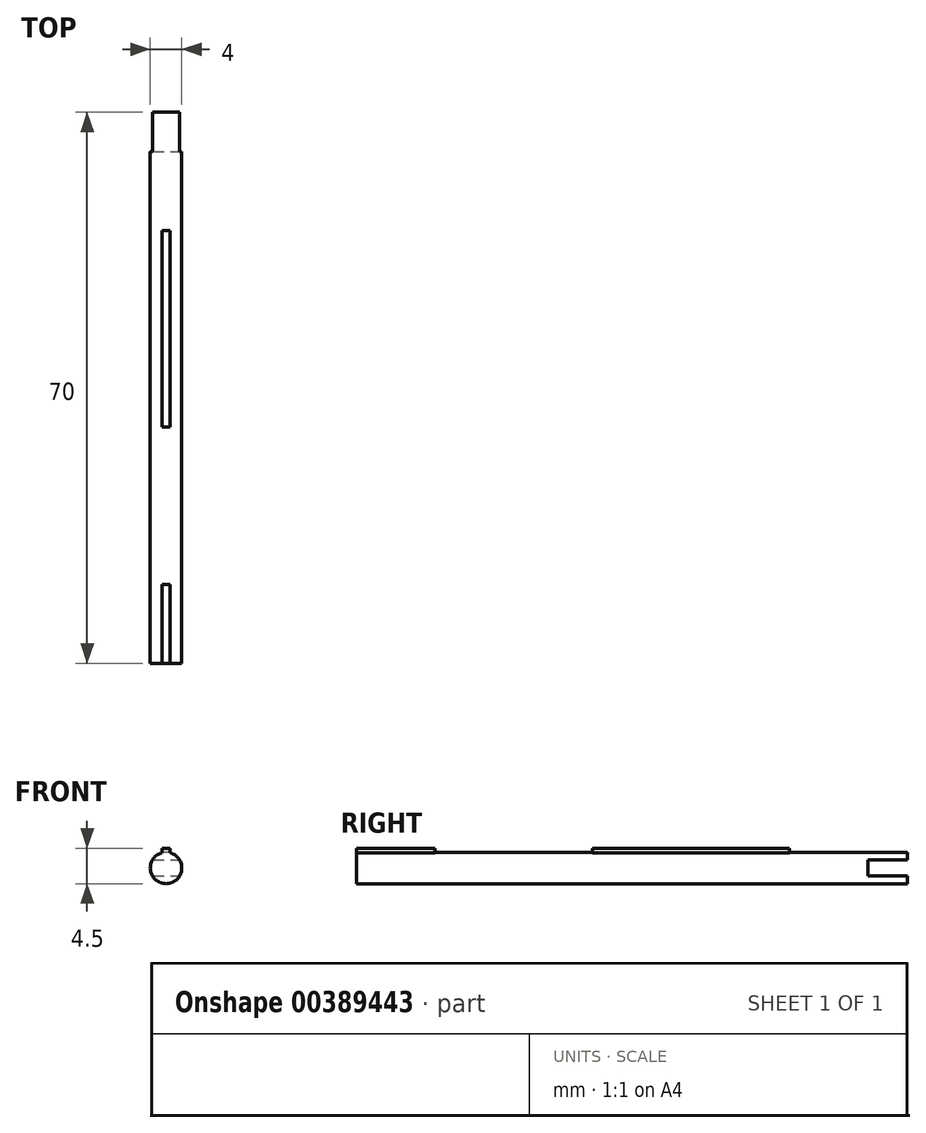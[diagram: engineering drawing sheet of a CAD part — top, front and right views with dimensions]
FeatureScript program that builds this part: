
annotation { "Feature Type Name" : "Feature", "Feature Type Description" : "" }
export const myFeature = defineFeature(function(context is Context, id is Id, definition is map)
    precondition{}
    {
        {
            var Q0;
            Q0=qCreatedBy(makeId("Front.planeOp"),FACE);
            var sketch = newSketch(context, id + "F0", { "sketchPlane" : qUnion([Q0])});
            skArc(sketch, "E0", {"start": v(-0.5, 1.94) * mm, "mid": v(0, -2) * mm, "end": v(0.5, 1.94) * mm});
            skLineSegment(sketch, "E1.bottom", {"start": v(0.5, 2.5) * mm, "end": v(-0.5, 2.5) * mm});
            skLineSegment(sketch, "E1.left", {"start": v(0.5, 2.5) * mm, "end": v(0.5, 1.94) * mm});
            skLineSegment(sketch, "E1.right", {"start": v(-0.5, 2.5) * mm, "end": v(-0.5, 1.94) * mm});
            skPoint(sketch, "E1.middle", {"position": v(0, 2) * mm});
            skPoint(sketch, "E2.orphan", {"position": v(-0.5, 1.5) * mm});
            skPoint(sketch, "E3.orphan", {"position": v(0.5, 1.5) * mm});
            skSolve(sketch);
        }
        {
            var Q0;
            Q0=qSketchRegion(id+"F0",true);
            var Q1;
            Q1=makeQuery(id+"F0.imprint","IMPRINT",FACE,{"disambiguationData":[TD([[makeQuery(id+"F0.imprint","IMPRINT",EDGE,{"derivedFrom":sQuery(id+"F0.wireOp",EDGE,"E0")}),1.0]])]});
            extrude(context, id + "F1", {"entities" : qUnion([Q0, Q1]), "depth" : 70 * mm});
        }
        {
            var Q0;
            Q0=makeQuery(id+"F1.opExtrude","CAP_FACE",FACE,{"disambiguationData":[OSD([sQuery(id+"F0.wireOp",EDGE,"E0"),sQuery(id+"F0.wireOp",EDGE,"E1.bottom"),sQuery(id+"F0.wireOp",EDGE,"E1.left"),sQuery(id+"F0.wireOp",EDGE,"E1.right")])],"isStart":false});
            cPlane(context, id + "F2", {"entities" : qUnion([Q0]), "cplaneType" : CPlaneType.OFFSET, "offset" : 10 * mm, "oppositeDirection" : true, "width" : 150 * mm, "height" : 150 * mm});
        }
        {
            var Q0;
            Q0=qCreatedBy(id+"F2.planeOp",FACE);
            var sketch = newSketch(context, id + "F3", { "sketchPlane" : qUnion([Q0])});
            skArc(sketch, "E4", {"start": v(0.5, 1.94) * mm, "mid": v(0, 2) * mm, "end": v(-0.5, 1.94) * mm});
            skLineSegment(sketch, "E5", {"start": v(-0.5, 2.5) * mm, "end": v(0.5, 2.5) * mm});
            skLineSegment(sketch, "E6", {"start": v(0.5, 1.94) * mm, "end": v(0.5, 2.5) * mm});
            skLineSegment(sketch, "E7", {"start": v(-0.5, 2.5) * mm, "end": v(-0.5, 1.94) * mm});
            skSolve(sketch);
        }
        {
            var Q0;
            Q0=makeQuery(id+"F3.imprint","IMPRINT",FACE,{"disambiguationData":[TD([[makeQuery(id+"F3.imprint","IMPRINT",EDGE,{"derivedFrom":sQuery(id+"F3.wireOp",EDGE,"E4")}),-1.0]])]});
            extrude(context, id + "F4", {"entities" : qUnion([Q0]), "operationType" : NewBodyOperationType.REMOVE, "oppositeDirection" : true, "depth" : 20 * mm});
        }
        {
            var Q0;
            Q0=makeQuery(id+"F1.opExtrude","CAP_FACE",FACE,{"disambiguationData":[OSD([sQuery(id+"F0.wireOp",EDGE,"E0"),sQuery(id+"F0.wireOp",EDGE,"E1.bottom"),sQuery(id+"F0.wireOp",EDGE,"E1.left"),sQuery(id+"F0.wireOp",EDGE,"E1.right")])],"isStart":true});
            var sketch = newSketch(context, id + "F5", { "sketchPlane" : qUnion([Q0])});
            skLineSegment(sketch, "E8", {"start": v(-0.5, 1.94) * mm, "end": v(-0.5, 2.5) * mm});
            skLineSegment(sketch, "E9", {"start": v(-0.5, 2.5) * mm, "end": v(0.5, 2.5) * mm});
            skLineSegment(sketch, "E10", {"start": v(0.5, 2.5) * mm, "end": v(0.5, 1.94) * mm});
            skArc(sketch, "E11", {"start": v(-0.5, 1.94) * mm, "mid": v(0, 2) * mm, "end": v(0.5, 1.94) * mm});
            skSolve(sketch);
        }
        {
            var Q0;
            Q0=makeQuery(id+"F5.imprint","IMPRINT",FACE,{"disambiguationData":[TD([[makeQuery(id+"F5.imprint","IMPRINT",EDGE,{"derivedFrom":sQuery(id+"F5.wireOp",EDGE,"E8")}),1.0]])]});
            extrude(context, id + "F6", {"entities" : qUnion([Q0]), "operationType" : NewBodyOperationType.REMOVE, "oppositeDirection" : true, "depth" : 15 * mm});
        }
        {
            var Q0;
            Q0=makeQuery(id+"F1.opExtrude","CAP_FACE",FACE,{"disambiguationData":[OSD([sQuery(id+"F0.wireOp",EDGE,"E0"),sQuery(id+"F0.wireOp",EDGE,"E1.bottom"),sQuery(id+"F0.wireOp",EDGE,"E1.left"),sQuery(id+"F0.wireOp",EDGE,"E1.right")])],"isStart":true});
            var sketch = newSketch(context, id + "F7", { "sketchPlane" : qUnion([Q0])});
            skLineSegment(sketch, "E12.bottom", {"start": v(3, 1) * mm, "end": v(-3, 1) * mm});
            skLineSegment(sketch, "E12.top", {"start": v(3, -1) * mm, "end": v(-3, -1) * mm});
            skLineSegment(sketch, "E12.left", {"start": v(3, 1) * mm, "end": v(3, -1) * mm});
            skLineSegment(sketch, "E12.right", {"start": v(-3, 1) * mm, "end": v(-3, -1) * mm});
            skPoint(sketch, "E12.middle", {"position": v(0, 0) * mm});
            skSolve(sketch);
        }
        {
            var Q0;
            Q0=qSketchRegion(id+"F7",true);
            extrude(context, id + "F8", {"entities" : qUnion([Q0]), "operationType" : NewBodyOperationType.REMOVE, "oppositeDirection" : true, "depth" : 5 * mm});
        }
    });
